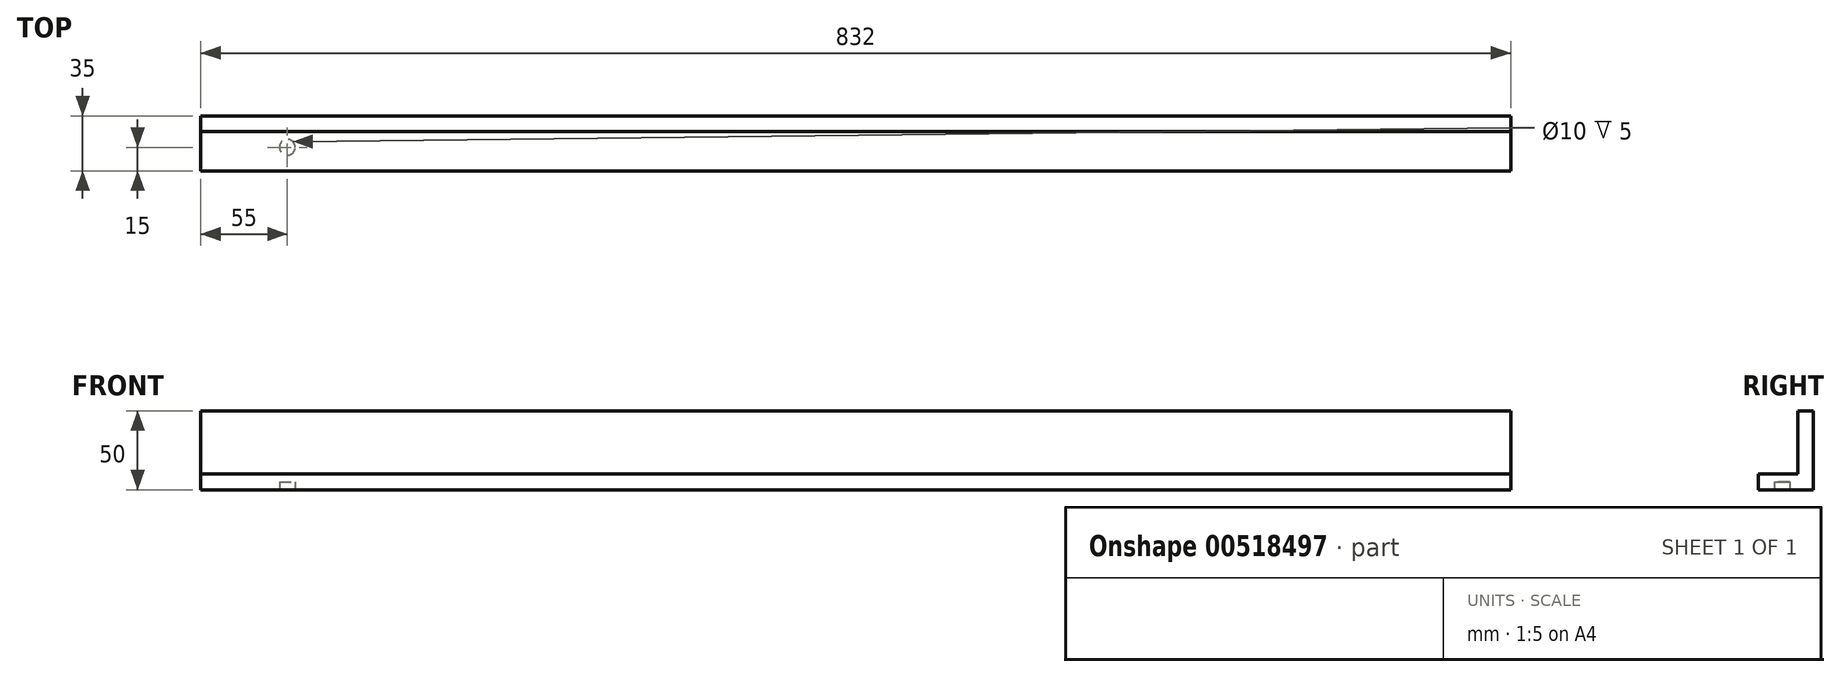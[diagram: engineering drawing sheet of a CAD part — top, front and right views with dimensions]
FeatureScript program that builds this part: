
annotation { "Feature Type Name" : "Feature", "Feature Type Description" : "" }
export const myFeature = defineFeature(function(context is Context, id is Id, definition is map)
    precondition{}
    {
        {
            var Q0;
            Q0=qCreatedBy(makeId("Right.planeOp"),FACE);
            var sketch = newSketch(context, id + "F0", { "sketchPlane" : qUnion([Q0])});
            skLineSegment(sketch, "E0", {"start": v(0, 0) * mm, "end": v(0, 50) * mm});
            skLineSegment(sketch, "E1", {"start": v(0, 50) * mm, "end": v(-10, 50) * mm});
            skLineSegment(sketch, "E2", {"start": v(-10, 50) * mm, "end": v(-10, 10) * mm});
            skLineSegment(sketch, "E3", {"start": v(-10, 10) * mm, "end": v(-35, 10) * mm});
            skLineSegment(sketch, "E4", {"start": v(-35, 10) * mm, "end": v(-35, 0) * mm});
            skLineSegment(sketch, "E5", {"start": v(-35, 0) * mm, "end": v(0, 0) * mm});
            skSolve(sketch);
        }
        {
            var Q0;
            Q0=makeQuery(id+"F0.imprint","IMPRINT",FACE,{"disambiguationData":[TD([[makeQuery(id+"F0.imprint","IMPRINT",EDGE,{"derivedFrom":sQuery(id+"F0.wireOp",EDGE,"E0")}),1.0]])]});
            extrude(context, id + "F1", {"entities" : qUnion([Q0]), "endBound" : BoundingType.SYMMETRIC, "depth" : 832 * mm, "offsetDistance" : 25 * mm});
        }
        {
            var Q0;
            Q0=makeQuery(id+"F1.opExtrude","SWEPT_FACE",FACE,{"disambiguationData":[OSD([sQuery(id+"F0.wireOp",EDGE,"E5")])]});
            var sketch = newSketch(context, id + "F2", { "sketchPlane" : qUnion([Q0])});
            skCircle(sketch, "E6", {"center": v(-361, 20) * mm, "radius": 5 * mm});
            skSolve(sketch);
        }
        {
            var Q0;
            Q0 = qSketchRegion(id + "F2", true);
            extrude(context, id + "F3", {"entities" : qUnion([Q0]), "operationType" : NewBodyOperationType.REMOVE, "oppositeDirection" : true, "depth" : 5 * mm, "offsetDistance" : 25 * mm});
        }
    });
